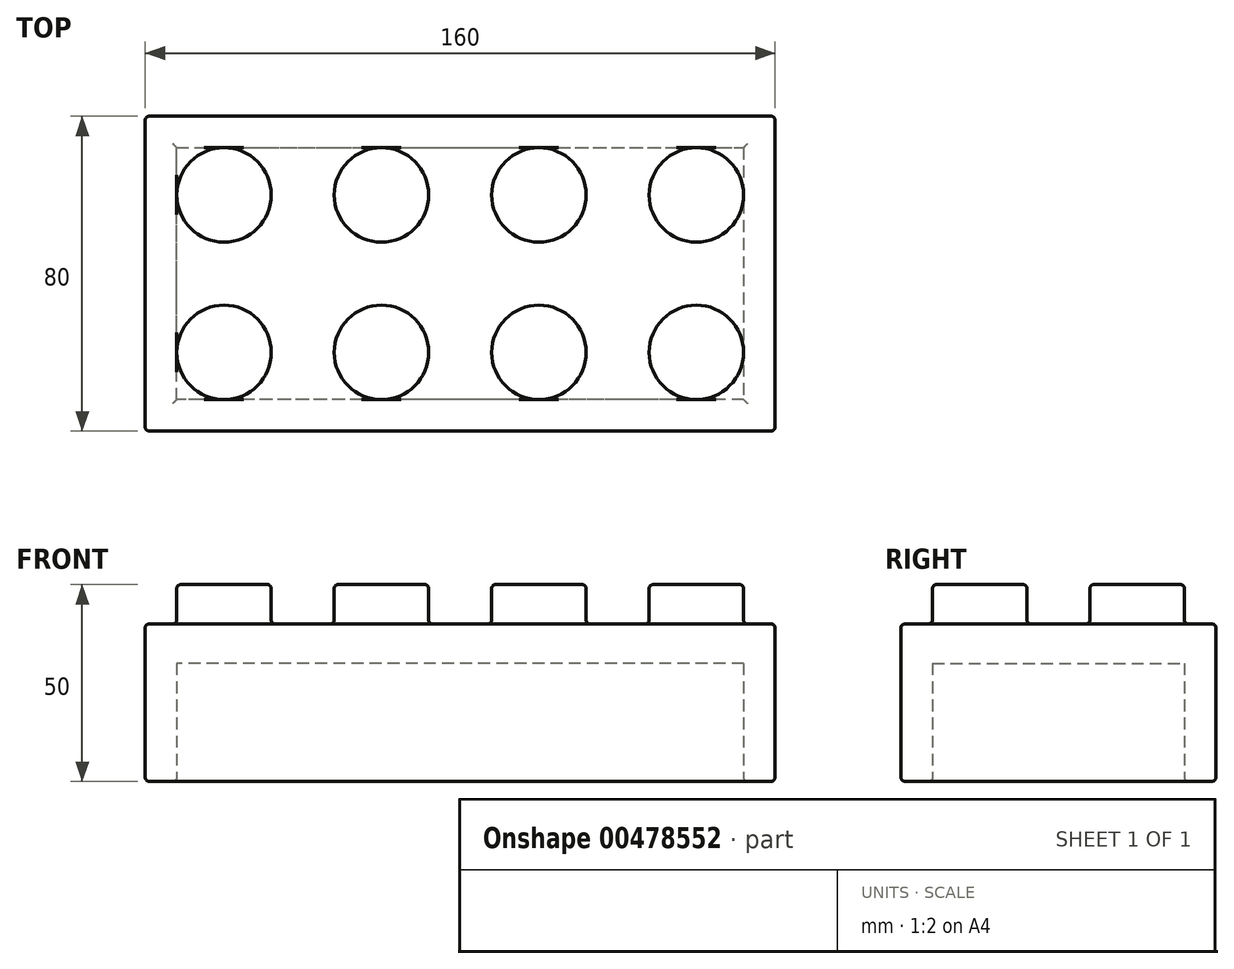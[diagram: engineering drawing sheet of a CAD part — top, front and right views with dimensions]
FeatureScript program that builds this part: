
annotation { "Feature Type Name" : "Feature", "Feature Type Description" : "" }
export const myFeature = defineFeature(function(context is Context, id is Id, definition is map)
    precondition{}
    {
        {
            var Q0;
            Q0=qCreatedBy(makeId("Top.planeOp"),FACE);
            var sketch = newSketch(context, id + "F0", { "sketchPlane" : qUnion([Q0])});
            skLineSegment(sketch, "E0.bottom", {"start": v(-75.4, 41.43) * mm, "end": v(84.6, 41.43) * mm});
            skLineSegment(sketch, "E0.top", {"start": v(-75.4, -38.57) * mm, "end": v(84.6, -38.57) * mm});
            skLineSegment(sketch, "E0.left", {"start": v(-75.4, 41.43) * mm, "end": v(-75.4, -38.57) * mm});
            skLineSegment(sketch, "E0.right", {"start": v(84.6, 41.43) * mm, "end": v(84.6, -38.57) * mm});
            skSolve(sketch);
        }
        {
            var Q0;
            Q0 = qSketchRegion(id + "F0", true);
            extrude(context, id + "F1", {"entities" : qUnion([Q0]), "depth" : 40 * mm});
        }
        {
            var Q0;
            Q0=makeQuery(id+"F1.opExtrude","CAP_FACE",FACE,{"disambiguationData":[OSD([sQuery(id+"F0.wireOp",EDGE,"E0.bottom"),sQuery(id+"F0.wireOp",EDGE,"E0.top"),sQuery(id+"F0.wireOp",EDGE,"E0.left"),sQuery(id+"F0.wireOp",EDGE,"E0.right")])],"isStart":true});
            var sketch = newSketch(context, id + "F2", { "sketchPlane" : qUnion([Q0])});
            skLineSegment(sketch, "E1.0", {"start": v(-67.4, 30.57) * mm, "end": v(-67.4, -33.43) * mm});
            skLineSegment(sketch, "E1.1", {"start": v(76.6, 30.57) * mm, "end": v(-67.4, 30.57) * mm});
            skLineSegment(sketch, "E1.2", {"start": v(76.6, -33.43) * mm, "end": v(76.6, 30.57) * mm});
            skLineSegment(sketch, "E1.3", {"start": v(-67.4, -33.43) * mm, "end": v(76.6, -33.43) * mm});
            skSolve(sketch);
        }
        {
            var Q0;
            Q0 = qSketchRegion(id + "F2", true);
            extrude(context, id + "F3", {"entities" : qUnion([Q0]), "operationType" : NewBodyOperationType.REMOVE, "oppositeDirection" : true, "depth" : 30 * mm});
        }
        {
            var Q0;
            Q0=makeQuery(id+"F1.opExtrude","CAP_FACE",FACE,{"disambiguationData":[OSD([sQuery(id+"F0.wireOp",EDGE,"E0.bottom"),sQuery(id+"F0.wireOp",EDGE,"E0.top"),sQuery(id+"F0.wireOp",EDGE,"E0.left"),sQuery(id+"F0.wireOp",EDGE,"E0.right")])],"isStart":false});
            var sketch = newSketch(context, id + "F4", { "sketchPlane" : qUnion([Q0])});
            skCircle(sketch, "E2", {"center": v(-55.4, 21.43) * mm, "radius": 12 * mm});
            skCircle(sketch, "E3.1.0.0", {"center": v(-15.4, 21.43) * mm, "radius": 12 * mm});
            skCircle(sketch, "E3.2.0.0", {"center": v(24.6, 21.43) * mm, "radius": 12 * mm});
            skCircle(sketch, "E3.3.0.0", {"center": v(64.6, 21.43) * mm, "radius": 12 * mm});
            skLineSegment(sketch, "E3.direction1", {"start": v(-55.4, 21.43) * mm, "end": v(-15.4, 21.43) * mm, "construction": true});
            skCircle(sketch, "E4", {"center": v(-55.4, -18.57) * mm, "radius": 12 * mm});
            skCircle(sketch, "E5.1.0.0", {"center": v(-15.4, -18.57) * mm, "radius": 12 * mm});
            skCircle(sketch, "E5.2.0.0", {"center": v(24.6, -18.57) * mm, "radius": 12 * mm});
            skCircle(sketch, "E5.3.0.0", {"center": v(64.6, -18.57) * mm, "radius": 12 * mm});
            skLineSegment(sketch, "E5.direction1", {"start": v(-55.4, -18.57) * mm, "end": v(-15.4, -18.57) * mm, "construction": true});
            skSolve(sketch);
        }
        {
            var Q0;
            Q0 = qSketchRegion(id + "F4", true);
            extrude(context, id + "F5", {"entities" : qUnion([Q0]), "operationType" : NewBodyOperationType.ADD, "depth" : 10 * mm});
        }
        {
            var Q0;
            Q0=makeQuery(id+"F5.opExtrude","CAP_FACE",FACE,{"disambiguationData":[OSD([sQuery(id+"F4.wireOp",EDGE,"E2")])],"isStart":false});
            var Q1;
            Q1=makeQuery(id+"F5.opExtrude","CAP_FACE",FACE,{"disambiguationData":[OSD([sQuery(id+"F4.wireOp",EDGE,"E3.1.0.0")])],"isStart":false});
            var Q2;
            Q2=makeQuery(id+"F5.opExtrude","CAP_EDGE",EDGE,{"disambiguationData":[OSD([sQuery(id+"F4.wireOp",EDGE,"E4")])],"isStart":false});
            var Q3;
            Q3=makeQuery(id+"F5.opExtrude","CAP_FACE",FACE,{"disambiguationData":[OSD([sQuery(id+"F4.wireOp",EDGE,"E5.1.0.0")])],"isStart":false});
            var Q4;
            Q4=makeQuery(id+"F5.opExtrude","CAP_FACE",FACE,{"disambiguationData":[OSD([sQuery(id+"F4.wireOp",EDGE,"E3.2.0.0")])],"isStart":false});
            var Q5;
            Q5=makeQuery(id+"F5.opExtrude","CAP_FACE",FACE,{"disambiguationData":[OSD([sQuery(id+"F4.wireOp",EDGE,"E3.3.0.0")])],"isStart":false});
            var Q6;
            Q6=makeQuery(id+"F5.opExtrude","CAP_FACE",FACE,{"disambiguationData":[OSD([sQuery(id+"F4.wireOp",EDGE,"E5.3.0.0")])],"isStart":false});
            var Q7;
            Q7=makeQuery(id+"F5.opExtrude","CAP_FACE",FACE,{"disambiguationData":[OSD([sQuery(id+"F4.wireOp",EDGE,"E5.2.0.0")])],"isStart":false});
            var Q8;
            Q8=makeQuery(id+"F5.opExtrude","CAP_FACE",FACE,{"disambiguationData":[OSD([sQuery(id+"F4.wireOp",EDGE,"E4")])],"isStart":false});
            fillet(context, id + "F6", {"entities" : qUnion([Q0, Q1, Q2, Q3, Q4, Q5, Q6, Q7, Q8]), "radius" : 1 * mm, "tangentPropagation" : true, "allowEdgeOverflow" : false});
        }
        {
            var Q0;
            Q0=makeQuery(id+"F1.opExtrude","CAP_FACE",FACE,{"disambiguationData":[OSD([sQuery(id+"F0.wireOp",EDGE,"E0.bottom"),sQuery(id+"F0.wireOp",EDGE,"E0.top"),sQuery(id+"F0.wireOp",EDGE,"E0.left"),sQuery(id+"F0.wireOp",EDGE,"E0.right")])],"isStart":false});
            fillet(context, id + "F7", {"entities" : qUnion([Q0]), "radius" : 1 * mm, "tangentPropagation" : true, "allowEdgeOverflow" : false});
        }
        {
            var Q0;
            Q0=makeQuery(id+"F1.opExtrude","SWEPT_FACE",FACE,{"disambiguationData":[OSD([sQuery(id+"F0.wireOp",EDGE,"E0.top")])]});
            fillet(context, id + "F8", {"entities" : qUnion([Q0]), "radius" : 1 * mm, "tangentPropagation" : true, "allowEdgeOverflow" : false});
        }
        {
            var Q0;
            Q0=makeQuery(id+"F1.opExtrude","SWEPT_FACE",FACE,{"disambiguationData":[OSD([sQuery(id+"F0.wireOp",EDGE,"E0.left")])]});
            fillet(context, id + "F9", {"entities" : qUnion([Q0]), "radius" : 1 * mm, "tangentPropagation" : true, "allowEdgeOverflow" : false});
        }
        {
            var Q0;
            Q0=makeQuery(id+"F1.opExtrude","SWEPT_FACE",FACE,{"disambiguationData":[OSD([sQuery(id+"F0.wireOp",EDGE,"E0.right")])]});
            fillet(context, id + "F10", {"entities" : qUnion([Q0]), "radius" : 1 * mm, "tangentPropagation" : true, "allowEdgeOverflow" : false});
        }
        {
            var Q0;
            Q0=makeQuery(id+"F1.opExtrude","CAP_FACE",FACE,{"disambiguationData":[OSD([sQuery(id+"F0.wireOp",EDGE,"E0.bottom"),sQuery(id+"F0.wireOp",EDGE,"E0.top"),sQuery(id+"F0.wireOp",EDGE,"E0.left"),sQuery(id+"F0.wireOp",EDGE,"E0.right")])],"isStart":true});
            fillet(context, id + "F11", {"entities" : qUnion([Q0]), "radius" : 1 * mm, "tangentPropagation" : true, "allowEdgeOverflow" : false});
        }
    });
